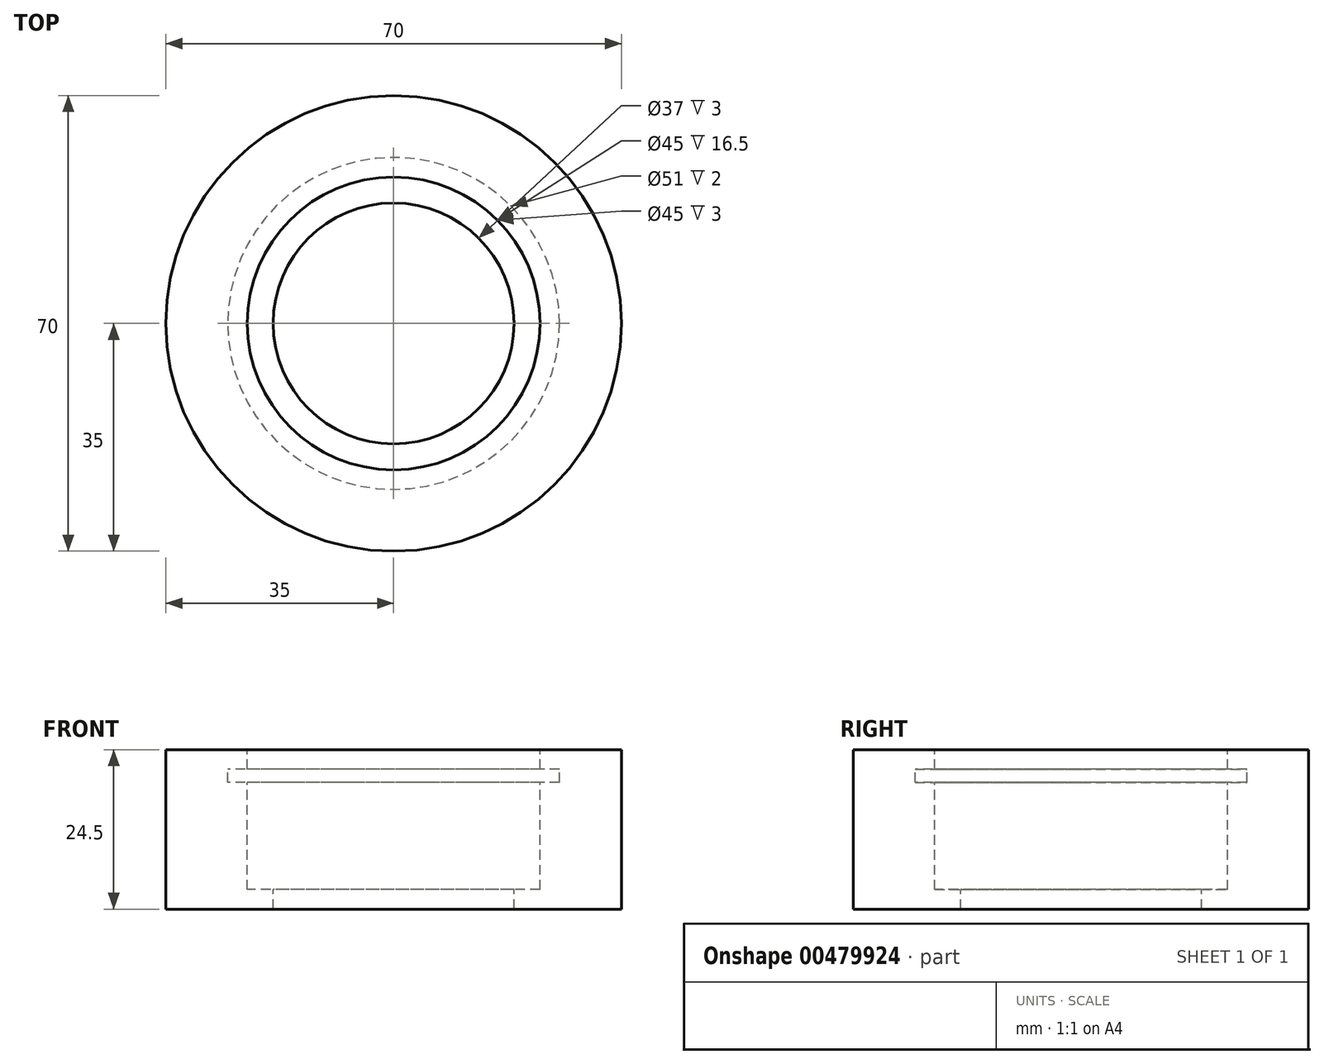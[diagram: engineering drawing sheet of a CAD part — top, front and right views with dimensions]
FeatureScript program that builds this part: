
annotation { "Feature Type Name" : "Feature", "Feature Type Description" : "" }
export const myFeature = defineFeature(function(context is Context, id is Id, definition is map)
    precondition{}
    {
        {
            var Q0;
            Q0=qCreatedBy(makeId("Front.planeOp"),FACE);
            var sketch = newSketch(context, id + "F0", { "sketchPlane" : qUnion([Q0])});
            skLineSegment(sketch, "E0", {"start": v(0, 0) * mm, "end": v(0, 24.5) * mm});
            skLineSegment(sketch, "E1", {"start": v(0, 24.5) * mm, "end": v(12.5, 24.5) * mm});
            skLineSegment(sketch, "E2", {"start": v(12.5, 24.5) * mm, "end": v(12.5, 21.5) * mm});
            skLineSegment(sketch, "E3", {"start": v(12.5, 21.5) * mm, "end": v(9.5, 21.5) * mm});
            skLineSegment(sketch, "E4", {"start": v(9.5, 21.5) * mm, "end": v(9.5, 19.5) * mm});
            skLineSegment(sketch, "E5", {"start": v(9.5, 19.5) * mm, "end": v(12.5, 19.5) * mm});
            skLineSegment(sketch, "E6", {"start": v(12.5, 19.5) * mm, "end": v(12.5, 3) * mm});
            skLineSegment(sketch, "E7", {"start": v(12.5, 3) * mm, "end": v(16.5, 3) * mm});
            skLineSegment(sketch, "E8", {"start": v(16.5, 3) * mm, "end": v(16.5, 0) * mm});
            skLineSegment(sketch, "E9", {"start": v(16.5, 0) * mm, "end": v(0, 0) * mm});
            skLineSegment(sketch, "E10", {"start": v(35, 24.5) * mm, "end": v(35, 0) * mm});
            skSolve(sketch);
        }
        {
            var Q0;
            Q0=makeQuery(id+"F0.imprint","IMPRINT",FACE,{"disambiguationData":[TD([[makeQuery(id+"F0.imprint","IMPRINT",EDGE,{"derivedFrom":sQuery(id+"F0.wireOp",EDGE,"E0")}),-1.0]])]});
            var Q1;
            Q1=sQuery(id+"F0.wireOp",EDGE,"E10");
            revolve(context, id + "F1", {"entities" : qUnion([Q0]), "axis" : qUnion([Q1]), "revolveType" : RevolveType.FULL});
        }
    });
